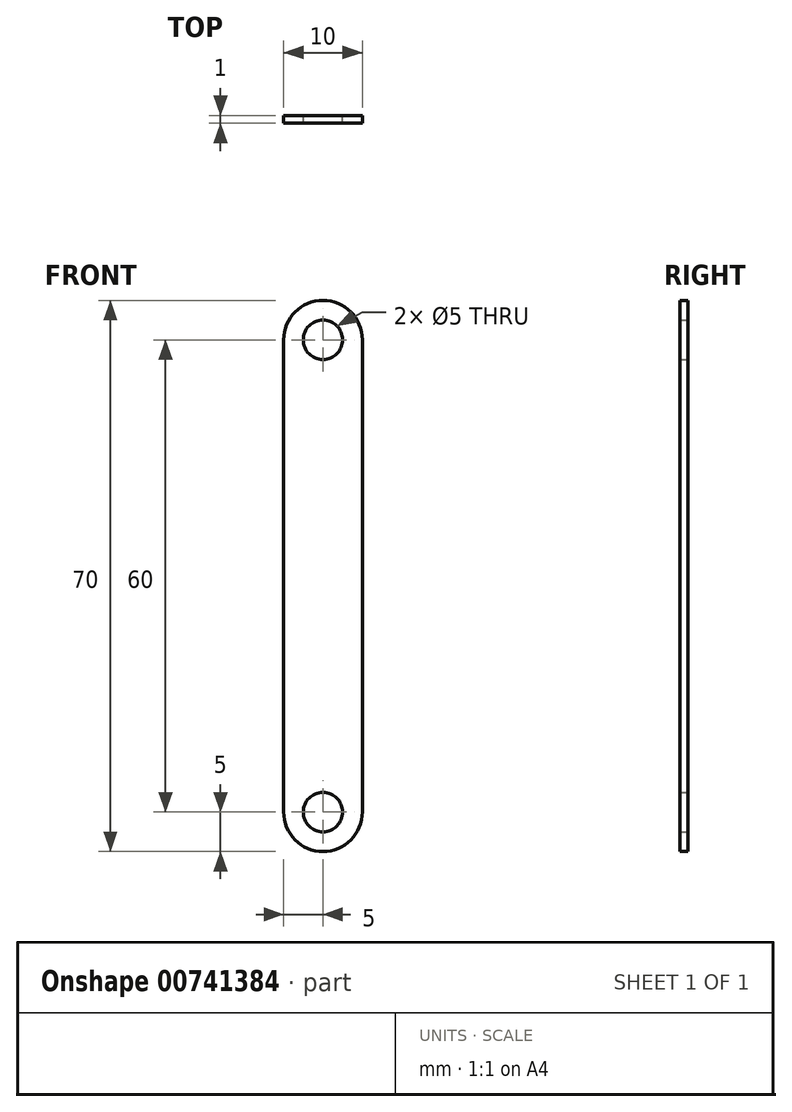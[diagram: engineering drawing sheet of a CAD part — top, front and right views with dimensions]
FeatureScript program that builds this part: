
annotation { "Feature Type Name" : "Feature", "Feature Type Description" : "" }
export const myFeature = defineFeature(function(context is Context, id is Id, definition is map)
    precondition{}
    {
        {
            var Q0;
            Q0=qCreatedBy(makeId("Front.planeOp"),FACE);
            var sketch = newSketch(context, id + "F0", { "sketchPlane" : qUnion([Q0])});
            skLineSegment(sketch, "E0", {"start": v(-8.59, 0) * mm, "end": v(8.84, 0) * mm, "construction": true});
            skCircle(sketch, "E1", {"center": v(0, 30) * mm, "radius": 5 * mm});
            skCircle(sketch, "E2", {"center": v(0, 30) * mm, "radius": 2.5 * mm});
            skCircle(sketch, "E3.MirrorC", {"center": v(0, -30) * mm, "radius": 5 * mm});
            skCircle(sketch, "E4.MirrorC", {"center": v(0, -30) * mm, "radius": 2.5 * mm});
            skLineSegment(sketch, "E5", {"start": v(-5, 30) * mm, "end": v(-5, -30) * mm});
            skLineSegment(sketch, "E6", {"start": v(5, 30) * mm, "end": v(5, -30) * mm});
            skSolve(sketch);
        }
        {
            var Q0;
            Q0 = qSketchRegion(id + "F0", true);
            extrude(context, id + "F1", {"entities" : qUnion([Q0]), "depth" : 1 * mm, "offsetDistance" : 25 * mm});
        }
    });
